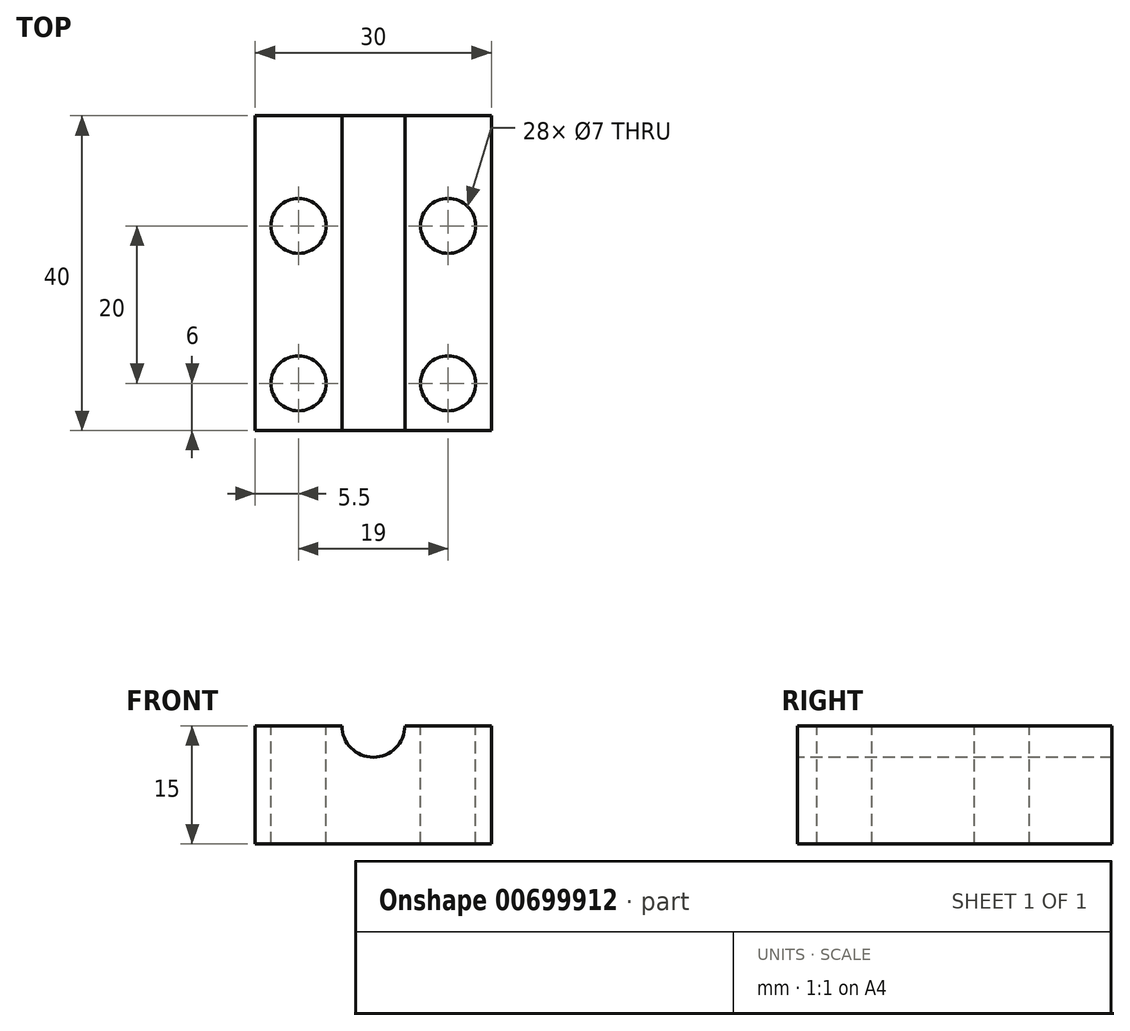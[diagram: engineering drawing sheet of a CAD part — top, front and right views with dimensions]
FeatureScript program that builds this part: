
annotation { "Feature Type Name" : "Feature", "Feature Type Description" : "" }
export const myFeature = defineFeature(function(context is Context, id is Id, definition is map)
    precondition{}
    {
        {
            var Q0;
            Q0=qCreatedBy(makeId("Top.planeOp"),FACE);
            var sketch = newSketch(context, id + "F0", { "sketchPlane" : qUnion([Q0])});
            skLineSegment(sketch, "E0.bottom", {"start": v(-15, 0) * mm, "end": v(15, 0) * mm});
            skLineSegment(sketch, "E0.top", {"start": v(-15, -40) * mm, "end": v(15, -40) * mm});
            skLineSegment(sketch, "E0.left", {"start": v(-15, 0) * mm, "end": v(-15, -40) * mm});
            skLineSegment(sketch, "E0.right", {"start": v(15, 0) * mm, "end": v(15, -40) * mm});
            skSolve(sketch);
        }
        {
            var Q0;
            Q0 = qSketchRegion(id + "F0", true);
            extrude(context, id + "F1", {"entities" : qUnion([Q0]), "depth" : 15 * mm, "offsetDistance" : 25 * mm});
        }
        {
            var Q0;
            Q0=makeQuery(id+"F1.opExtrude","SWEPT_FACE",FACE,{"disambiguationData":[OSD([sQuery(id+"F0.wireOp",EDGE,"E0.top")])]});
            var sketch = newSketch(context, id + "F2", { "sketchPlane" : qUnion([Q0])});
            skArc(sketch, "E1", {"start": v(4, 15) * mm, "mid": v(0, 11) * mm, "end": v(-4, 15) * mm});
            skLineSegment(sketch, "E2", {"start": v(-4, 15) * mm, "end": v(4, 15) * mm});
            skSolve(sketch);
        }
        {
            var Q0;
            Q0 = qSketchRegion(id + "F2", true);
            extrude(context, id + "F3", {"entities" : qUnion([Q0]), "operationType" : NewBodyOperationType.REMOVE, "endBound" : BoundingType.UP_TO_NEXT, "oppositeDirection" : true, "depth" : 25 * mm, "offsetDistance" : 25 * mm});
        }
        {
            var Q0;
            {var subQ0=sQuery(id+"F0.wireOp",EDGE,"E0.bottom");var subQ1=sQuery(id+"F0.wireOp",EDGE,"E0.top");var subQ2=sQuery(id+"F0.wireOp",EDGE,"E0.left");Q0=makeQuery(id+"F3.boolean.opBoolean","SPLIT",FACE,{"disambiguationData":[TD([makeQuery(id+"F1.opExtrude","SWEPT_FACE",FACE,{"disambiguationData":[OSD([subQ2])]})])],"derivedFrom":makeQuery(id+"F1.opExtrude","CAP_FACE",FACE,{"disambiguationData":[OSD([subQ0,subQ1,subQ2,sQuery(id+"F0.wireOp",EDGE,"E0.right")])],"isStart":false})});}
            var sketch = newSketch(context, id + "F4", { "sketchPlane" : qUnion([Q0])});
            skCircle(sketch, "E3", {"center": v(-9.5, -34) * mm, "radius": 3.5 * mm});
            skCircle(sketch, "E4", {"center": v(-9.5, -14) * mm, "radius": 3.5 * mm});
            skCircle(sketch, "E5", {"center": v(9.5, -14) * mm, "radius": 3.5 * mm});
            skCircle(sketch, "E6", {"center": v(9.5, -34) * mm, "radius": 3.5 * mm});
            skSolve(sketch);
        }
        {
            var Q0;
            Q0 = qSketchRegion(id + "F4", true);
            extrude(context, id + "F5", {"entities" : qUnion([Q0]), "operationType" : NewBodyOperationType.REMOVE, "endBound" : BoundingType.UP_TO_NEXT, "oppositeDirection" : true, "depth" : 25 * mm, "offsetDistance" : 25 * mm});
        }
    });
